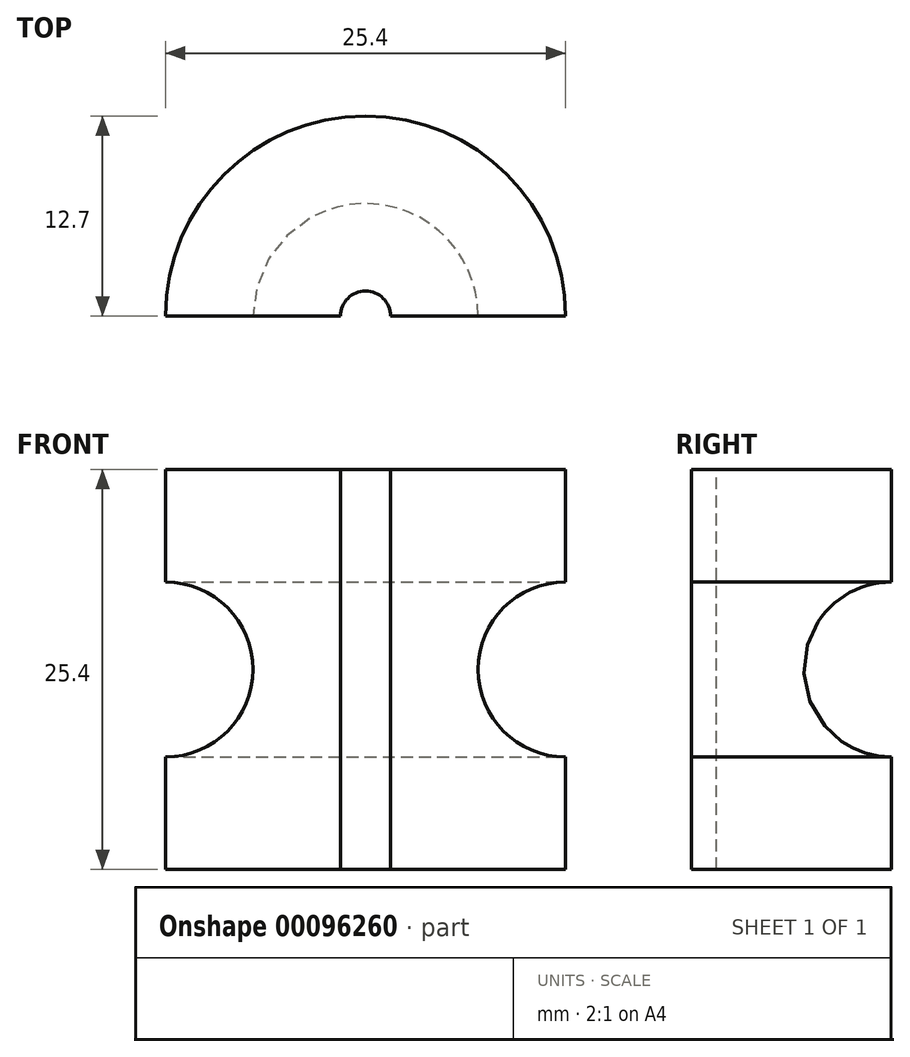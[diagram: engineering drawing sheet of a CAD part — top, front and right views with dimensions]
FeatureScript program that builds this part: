
annotation { "Feature Type Name" : "Feature", "Feature Type Description" : "" }
export const myFeature = defineFeature(function(context is Context, id is Id, definition is map)
    precondition{}
    {
        {
            var Q0;
            Q0=qCreatedBy(makeId("Front.planeOp"),FACE);
            var sketch = newSketch(context, id + "F0", { "sketchPlane" : qUnion([Q0])});
            skLineSegment(sketch, "E0.bottom", {"start": v(0, 0) * mm, "end": v(12.7, 0) * mm});
            skLineSegment(sketch, "E0.top", {"start": v(0, 25.4) * mm, "end": v(12.7, 25.4) * mm});
            skLineSegment(sketch, "E0.left", {"start": v(0, 0) * mm, "end": v(0, 25.4) * mm});
            skLineSegment(sketch, "E0.right", {"start": v(12.7, 0) * mm, "end": v(12.7, 25.4) * mm});
            skCircle(sketch, "E1", {"center": v(0, 12.7) * mm, "radius": 5.56 * mm});
            skSolve(sketch);
        }
        {
            var Q0;
            {var subQ4=sQuery(id+"F0.wireOp",EDGE,"E0.bottom");Q0=makeQuery(id+"F0.imprint","IMPRINT",FACE,{"disambiguationData":[TD([[makeQuery(id+"F0.imprint","IMPRINT",EDGE,{"derivedFrom":subQ4}),1.0]])]});}
            var Q1;
            Q1=sQuery(id+"F0.wireOp",EDGE,"E0.right");
            revolve(context, id + "F1", {"entities" : qUnion([Q0]), "axis" : qUnion([Q1]), "revolveType" : RevolveType.FULL});
        }
        {
            var Q0;
            Q0=makeQuery(id+"F1.opRevolve","SWEPT_FACE",FACE,{"disambiguationData":[OSD([sQuery(id+"F0.wireOp",EDGE,"E0.top")])]});
            var sketch = newSketch(context, id + "F2", { "sketchPlane" : qUnion([Q0])});
            skLineSegment(sketch, "E2", {"start": v(0, 0) * mm, "end": v(25.4, 0) * mm});
            skLineSegment(sketch, "E3", {"start": v(12.7, 0) * mm, "end": v(12.7, 12.7) * mm});
            skCircle(sketch, "E4", {"center": v(12.7, 0) * mm, "radius": 1.59 * mm});
            skSolve(sketch);
        }
        {
            var Q0;
            Q0 = qSketchRegion(id + "F2", true);
            var Q1;
            {var subQ3=sQuery(id+"F2.wireOp",EDGE,"E3");Q1=makeQuery(id+"F2.imprint","IMPRINT",FACE,{"disambiguationData":[TD([[makeQuery(id+"F2.imprint","IMPRINT",EDGE,{"derivedFrom":subQ3}),-1.0]])]});}
            var Q2;
            {var subQ0=sQuery(id+"F2.wireOp",EDGE,"E2");var subQ3=sQuery(id+"F2.wireOp",EDGE,"E4");var subQ4=makeQuery(id+"F2.imprint","INTERSECT",VERTEX,{"disambiguationData":[OD(1.0)],"derivedFrom":[subQ0,subQ3]});Q2=makeQuery(id+"F2.imprint","IMPRINT",FACE,{"disambiguationData":[TD([[makeQuery(id+"F2.imprint","IMPRINT",EDGE,{"disambiguationData":[TD([[subQ4,-1.0]])],"derivedFrom":subQ3}),-1.0]])]});}
            extrude(context, id + "F3", {"entities" : qUnion([Q0, Q1, Q2]), "operationType" : NewBodyOperationType.REMOVE, "endBound" : BoundingType.THROUGH_ALL, "oppositeDirection" : true, "depth" : 25.4 * mm});
        }
    });
